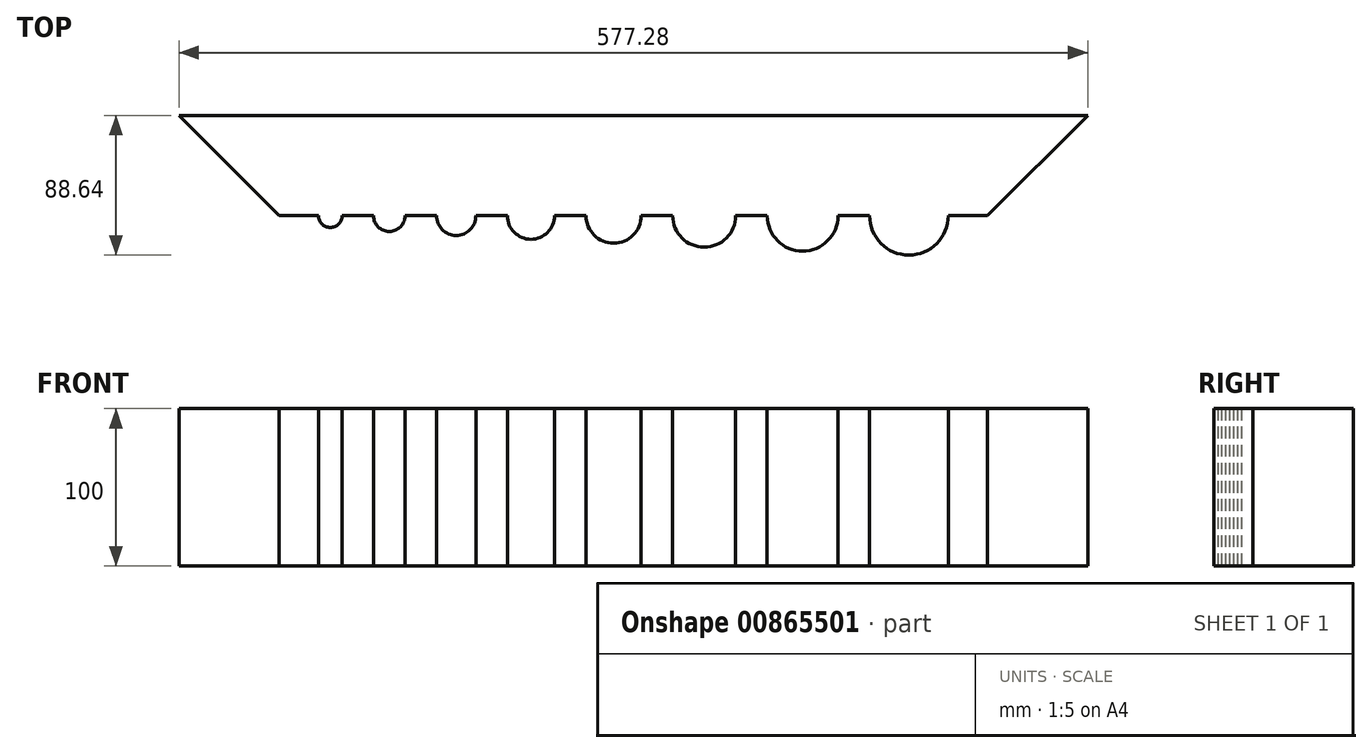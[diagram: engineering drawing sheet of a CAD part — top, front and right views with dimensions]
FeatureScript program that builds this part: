
annotation { "Feature Type Name" : "Feature", "Feature Type Description" : "" }
export const myFeature = defineFeature(function(context is Context, id is Id, definition is map)
    precondition{}
    {
        {
            var Q0;
            Q0=qCreatedBy(makeId("Top.planeOp"),FACE);
            var sketch = newSketch(context, id + "F0", { "sketchPlane" : qUnion([Q0])});
            skLineSegment(sketch, "E0.bottom", {"start": v(0, 0) * mm, "end": v(450, 0) * mm});
            skLineSegment(sketch, "E0.top", {"start": v(0, -450) * mm, "end": v(450, -450) * mm});
            skLineSegment(sketch, "E0.left", {"start": v(0, 0) * mm, "end": v(0, -450) * mm});
            skLineSegment(sketch, "E0.right", {"start": v(450, 0) * mm, "end": v(450, -450) * mm});
            skCircle(sketch, "E1", {"center": v(32.5, 0) * mm, "radius": 7.5 * mm});
            skCircle(sketch, "E2", {"center": v(70, 0) * mm, "radius": 10 * mm});
            skCircle(sketch, "E3", {"center": v(112.5, 0) * mm, "radius": 12.5 * mm});
            skCircle(sketch, "E4", {"center": v(212.5, 0) * mm, "radius": 17.5 * mm});
            skCircle(sketch, "E5", {"center": v(270, 0) * mm, "radius": 20 * mm});
            skPoint(sketch, "E6", {"position": v(0, -225) * mm});
            skCircle(sketch, "E7", {"center": v(160, 0) * mm, "radius": 15 * mm});
            skCircle(sketch, "E8", {"center": v(332.5, 0) * mm, "radius": 22.5 * mm});
            skCircle(sketch, "E9", {"center": v(400, 0) * mm, "radius": 25 * mm});
            skCircle(sketch, "E10", {"center": v(0, -50) * mm, "radius": 27.5 * mm});
            skCircle(sketch, "E11", {"center": v(0, -127.5) * mm, "radius": 30 * mm});
            skCircle(sketch, "E12", {"center": v(0, -210) * mm, "radius": 32.5 * mm});
            skCircle(sketch, "E13", {"center": v(0, -297.5) * mm, "radius": 35 * mm});
            skCircle(sketch, "E14", {"center": v(0, -390) * mm, "radius": 37.5 * mm});
            skCircle(sketch, "E15.cCircle", {"center": v(450, -45) * mm, "radius": 20 * mm, "construction": true});
            skLineSegment(sketch, "E15.0", {"start": v(450, -65) * mm, "end": v(432.68, -55) * mm});
            skLineSegment(sketch, "E15.1", {"start": v(432.68, -55) * mm, "end": v(432.68, -35) * mm});
            skLineSegment(sketch, "E15.2", {"start": v(432.68, -35) * mm, "end": v(450, -25) * mm});
            skLineSegment(sketch, "E15.3", {"start": v(450, -25) * mm, "end": v(467.32, -35) * mm});
            skLineSegment(sketch, "E15.4", {"start": v(467.32, -35) * mm, "end": v(467.32, -55) * mm});
            skLineSegment(sketch, "E15.5", {"start": v(467.32, -55) * mm, "end": v(450, -65) * mm});
            skCircle(sketch, "E16.cCircle", {"center": v(450, -120) * mm, "radius": 34.64 * mm, "construction": true});
            skLineSegment(sketch, "E16.0", {"start": v(420.17, -137.61) * mm, "end": v(419.83, -102.97) * mm});
            skLineSegment(sketch, "E16.1", {"start": v(419.83, -102.97) * mm, "end": v(449.66, -85.36) * mm});
            skLineSegment(sketch, "E16.2", {"start": v(449.66, -85.36) * mm, "end": v(479.83, -102.39) * mm});
            skLineSegment(sketch, "E16.3", {"start": v(479.83, -102.39) * mm, "end": v(480.17, -137.03) * mm});
            skLineSegment(sketch, "E16.4", {"start": v(480.17, -137.03) * mm, "end": v(450.34, -154.64) * mm});
            skLineSegment(sketch, "E16.5", {"start": v(450.34, -154.64) * mm, "end": v(420.17, -137.61) * mm});
            skCircle(sketch, "E17.cCircle", {"center": v(450, -225) * mm, "radius": 46.19 * mm, "construction": true});
            skLineSegment(sketch, "E17.0", {"start": v(410.35, -248.7) * mm, "end": v(409.66, -202.51) * mm});
            skLineSegment(sketch, "E17.1", {"start": v(409.66, -202.51) * mm, "end": v(449.3, -178.82) * mm});
            skLineSegment(sketch, "E17.2", {"start": v(449.3, -178.82) * mm, "end": v(489.65, -201.3) * mm});
            skLineSegment(sketch, "E17.3", {"start": v(489.65, -201.3) * mm, "end": v(490.34, -247.49) * mm});
            skLineSegment(sketch, "E17.4", {"start": v(490.34, -247.49) * mm, "end": v(450.7, -271.18) * mm});
            skLineSegment(sketch, "E17.5", {"start": v(450.7, -271.18) * mm, "end": v(410.35, -248.7) * mm});
            skCircle(sketch, "E18.cCircle", {"center": v(450, -360) * mm, "radius": 57.74 * mm, "construction": true});
            skLineSegment(sketch, "E18.0", {"start": v(400.24, -330.72) * mm, "end": v(450.48, -302.27) * mm});
            skLineSegment(sketch, "E18.1", {"start": v(450.48, -302.27) * mm, "end": v(500.24, -331.55) * mm});
            skLineSegment(sketch, "E18.2", {"start": v(500.24, -331.55) * mm, "end": v(499.76, -389.28) * mm});
            skLineSegment(sketch, "E18.3", {"start": v(499.76, -389.28) * mm, "end": v(449.52, -417.73) * mm});
            skLineSegment(sketch, "E18.4", {"start": v(449.52, -417.73) * mm, "end": v(399.76, -388.45) * mm});
            skLineSegment(sketch, "E18.5", {"start": v(399.76, -388.45) * mm, "end": v(400.24, -330.72) * mm});
            skLineSegment(sketch, "E19", {"start": v(420, -450) * mm, "end": v(412.5, -437) * mm});
            skLineSegment(sketch, "E20", {"start": v(412.5, -437) * mm, "end": v(405, -450) * mm});
            skLineSegment(sketch, "E21", {"start": v(420, -450) * mm, "end": v(405, -450) * mm});
            skLineSegment(sketch, "E22", {"start": v(375, -450) * mm, "end": v(362.5, -428.35) * mm});
            skLineSegment(sketch, "E23", {"start": v(362.5, -428.35) * mm, "end": v(350, -450) * mm});
            skLineSegment(sketch, "E24", {"start": v(350, -450) * mm, "end": v(375, -450) * mm});
            skLineSegment(sketch, "E25", {"start": v(320, -450) * mm, "end": v(305, -424.02) * mm});
            skLineSegment(sketch, "E26", {"start": v(305, -424.02) * mm, "end": v(290, -450) * mm});
            skLineSegment(sketch, "E27", {"start": v(290, -450) * mm, "end": v(320, -450) * mm});
            skLineSegment(sketch, "E28", {"start": v(260, -450) * mm, "end": v(220, -450) * mm});
            skLineSegment(sketch, "E29", {"start": v(220, -450) * mm, "end": v(240, -415.36) * mm});
            skLineSegment(sketch, "E30", {"start": v(240, -415.36) * mm, "end": v(260, -450) * mm});
            skLineSegment(sketch, "E31", {"start": v(190, -450) * mm, "end": v(140, -450) * mm});
            skLineSegment(sketch, "E32", {"start": v(140, -450) * mm, "end": v(165, -406.7) * mm});
            skLineSegment(sketch, "E33", {"start": v(165, -406.7) * mm, "end": v(190, -450) * mm});
            skLineSegment(sketch, "E34", {"start": v(110, -450) * mm, "end": v(50, -450) * mm});
            skLineSegment(sketch, "E35", {"start": v(50, -450) * mm, "end": v(80, -398.04) * mm});
            skLineSegment(sketch, "E36", {"start": v(80, -398.04) * mm, "end": v(110, -450) * mm});
            skCircle(sketch, "E37", {"center": v(366.86, -63.19) * mm, "radius": 8.5 * mm});
            skCircle(sketch, "E38", {"center": v(306.86, -63.19) * mm, "radius": 11.5 * mm});
            skCircle(sketch, "E39", {"center": v(237.86, -63.19) * mm, "radius": 17.5 * mm});
            skCircle(sketch, "E40", {"center": v(172.86, -63.19) * mm, "radius": 22.5 * mm});
            skCircle(sketch, "E41", {"center": v(90.36, -63.19) * mm, "radius": 30 * mm});
            skPoint(sketch, "E42.cornerSnap0", {"position": v(400, -359.59) * mm});
            skEllipse(sketch, "E43", {"center": v(355, -158.3) * mm, "majorRadius": 69.57 * mm, "minorRadius": 24.91 * mm, "majorAxis": v(0, -1)});
            skEllipse(sketch, "E44", {"center": v(255, -158.3) * mm, "majorRadius": 57.98 * mm, "minorRadius": 25.3 * mm, "majorAxis": v(0, -1)});
            skEllipse(sketch, "E45", {"center": v(160, -158.3) * mm, "majorRadius": 47.06 * mm, "minorRadius": 19.98 * mm, "majorAxis": v(0, -1)});
            skEllipse(sketch, "E46", {"center": v(75, -158.3) * mm, "majorRadius": 42.97 * mm, "minorRadius": 16.37 * mm, "majorAxis": v(0, -1)});
            skLineSegment(sketch, "E47.bottom", {"start": v(132.9, -316.06) * mm, "end": v(52.9, -316.06) * mm});
            skLineSegment(sketch, "E47.top", {"start": v(132.9, -236.06) * mm, "end": v(52.9, -236.06) * mm});
            skLineSegment(sketch, "E47.left", {"start": v(132.9, -316.06) * mm, "end": v(132.9, -236.06) * mm});
            skLineSegment(sketch, "E47.right", {"start": v(52.9, -316.06) * mm, "end": v(52.9, -236.06) * mm});
            skPoint(sketch, "E47.middle", {"position": v(92.9, -276.06) * mm});
            skLineSegment(sketch, "E48.bottom", {"start": v(232.94, -306.06) * mm, "end": v(172.94, -306.06) * mm});
            skLineSegment(sketch, "E48.top", {"start": v(232.94, -246.06) * mm, "end": v(172.94, -246.06) * mm});
            skLineSegment(sketch, "E48.left", {"start": v(232.94, -306.06) * mm, "end": v(232.94, -246.06) * mm});
            skLineSegment(sketch, "E48.right", {"start": v(172.94, -306.06) * mm, "end": v(172.94, -246.06) * mm});
            skPoint(sketch, "E48.middle", {"position": v(202.94, -276.06) * mm});
            skLineSegment(sketch, "E49.bottom", {"start": v(312.28, -296.06) * mm, "end": v(272.28, -296.06) * mm});
            skLineSegment(sketch, "E49.top", {"start": v(312.28, -256.06) * mm, "end": v(272.28, -256.06) * mm});
            skLineSegment(sketch, "E49.left", {"start": v(312.28, -296.06) * mm, "end": v(312.28, -256.06) * mm});
            skLineSegment(sketch, "E49.right", {"start": v(272.28, -296.06) * mm, "end": v(272.28, -256.06) * mm});
            skPoint(sketch, "E49.middle", {"position": v(292.28, -276.06) * mm});
            skLineSegment(sketch, "E50.bottom", {"start": v(372.3, -286.06) * mm, "end": v(352.3, -286.06) * mm});
            skLineSegment(sketch, "E50.top", {"start": v(372.3, -266.06) * mm, "end": v(352.3, -266.06) * mm});
            skLineSegment(sketch, "E50.left", {"start": v(372.3, -286.06) * mm, "end": v(372.3, -266.06) * mm});
            skLineSegment(sketch, "E50.right", {"start": v(352.3, -286.06) * mm, "end": v(352.3, -266.06) * mm});
            skPoint(sketch, "E50.middle", {"position": v(362.3, -276.06) * mm});
            skLineSegment(sketch, "E51.bottom", {"start": v(80, -382.47) * mm, "end": v(60, -382.47) * mm});
            skLineSegment(sketch, "E51.top", {"start": v(80, -372.47) * mm, "end": v(60, -372.47) * mm});
            skLineSegment(sketch, "E51.left", {"start": v(80, -382.47) * mm, "end": v(80, -372.47) * mm});
            skLineSegment(sketch, "E51.right", {"start": v(60, -382.47) * mm, "end": v(60, -372.47) * mm});
            skPoint(sketch, "E51.middle", {"position": v(70, -377.47) * mm});
            skLineSegment(sketch, "E52.bottom", {"start": v(110, -387.47) * mm, "end": v(150, -387.47) * mm});
            skLineSegment(sketch, "E52.top", {"start": v(110, -367.47) * mm, "end": v(150, -367.47) * mm});
            skLineSegment(sketch, "E52.left", {"start": v(110, -387.47) * mm, "end": v(110, -367.47) * mm});
            skLineSegment(sketch, "E52.right", {"start": v(150, -387.47) * mm, "end": v(150, -367.47) * mm});
            skPoint(sketch, "E52.middle", {"position": v(130, -377.47) * mm});
            skLineSegment(sketch, "E53.bottom", {"start": v(190, -392.47) * mm, "end": v(250, -392.47) * mm});
            skLineSegment(sketch, "E53.top", {"start": v(190, -362.47) * mm, "end": v(250, -362.47) * mm});
            skLineSegment(sketch, "E53.left", {"start": v(190, -392.47) * mm, "end": v(190, -362.47) * mm});
            skLineSegment(sketch, "E53.right", {"start": v(250, -392.47) * mm, "end": v(250, -362.47) * mm});
            skPoint(sketch, "E53.middle", {"position": v(220, -377.47) * mm});
            skLineSegment(sketch, "E54.bottom", {"start": v(375, -397.47) * mm, "end": v(295, -397.47) * mm});
            skLineSegment(sketch, "E54.top", {"start": v(375, -357.47) * mm, "end": v(295, -357.47) * mm});
            skLineSegment(sketch, "E54.left", {"start": v(375, -397.47) * mm, "end": v(375, -357.47) * mm});
            skLineSegment(sketch, "E54.right", {"start": v(295, -397.47) * mm, "end": v(295, -357.47) * mm});
            skPoint(sketch, "E54.middle", {"position": v(335, -377.47) * mm});
            skLineSegment(sketch, "E55", {"start": v(0, 0) * mm, "end": v(-63.64, 63.64) * mm});
            skLineSegment(sketch, "E56", {"start": v(-63.64, 63.64) * mm, "end": v(513.64, 63.64) * mm});
            skLineSegment(sketch, "E57", {"start": v(513.64, 63.64) * mm, "end": v(450, 0) * mm});
            skLineSegment(sketch, "E58", {"start": v(513.64, 63.64) * mm, "end": v(513.64, -513.64) * mm});
            skLineSegment(sketch, "E59", {"start": v(513.64, -513.64) * mm, "end": v(450, -450) * mm});
            skLineSegment(sketch, "E60", {"start": v(-63.64, 63.64) * mm, "end": v(-63.64, -513.64) * mm});
            skLineSegment(sketch, "E61", {"start": v(-63.64, -513.64) * mm, "end": v(0, -450) * mm});
            skLineSegment(sketch, "E62", {"start": v(-63.64, -513.64) * mm, "end": v(513.64, -513.64) * mm});
            skSolve(sketch);
        }
        {
            var Q0;
            {var subQ20=sQuery(id+"F0.wireOp",EDGE,"E55");Q0=makeQuery(id+"F0.imprint","IMPRINT",FACE,{"disambiguationData":[TD([[makeQuery(id+"F0.imprint","IMPRINT",EDGE,{"derivedFrom":subQ20}),-1.0]])]});}
            var Q1;
            {var subQ0=sQuery(id+"F0.wireOp",EDGE,"E1");var subQ1=sQuery(id+"F0.wireOp",EDGE,"E0.bottom");var subQ2=makeQuery(id+"F0.imprint","INTERSECT",VERTEX,{"disambiguationData":[OD(0.0)],"derivedFrom":[subQ1,subQ0]});Q1=makeQuery(id+"F0.imprint","IMPRINT",FACE,{"disambiguationData":[TD([[makeQuery(id+"F0.imprint","IMPRINT",EDGE,{"disambiguationData":[TD([[subQ2,-1.0]])],"derivedFrom":subQ1}),1.0]])]});}
            var Q2;
            {var subQ0=sQuery(id+"F0.wireOp",EDGE,"E1");var subQ1=sQuery(id+"F0.wireOp",EDGE,"E0.bottom");var subQ2=makeQuery(id+"F0.imprint","INTERSECT",VERTEX,{"disambiguationData":[OD(0.0)],"derivedFrom":[subQ1,subQ0]});Q2=makeQuery(id+"F0.imprint","IMPRINT",FACE,{"disambiguationData":[TD([[makeQuery(id+"F0.imprint","IMPRINT",EDGE,{"disambiguationData":[TD([[subQ2,-1.0]])],"derivedFrom":subQ1}),-1.0]])]});}
            var Q3;
            {var subQ0=sQuery(id+"F0.wireOp",EDGE,"E2");var subQ1=sQuery(id+"F0.wireOp",EDGE,"E0.bottom");var subQ2=makeQuery(id+"F0.imprint","INTERSECT",VERTEX,{"disambiguationData":[OD(0.0)],"derivedFrom":[subQ1,subQ0]});Q3=makeQuery(id+"F0.imprint","IMPRINT",FACE,{"disambiguationData":[TD([[makeQuery(id+"F0.imprint","IMPRINT",EDGE,{"disambiguationData":[TD([[subQ2,-1.0]])],"derivedFrom":subQ1}),1.0]])]});}
            var Q4;
            {var subQ0=sQuery(id+"F0.wireOp",EDGE,"E2");var subQ1=sQuery(id+"F0.wireOp",EDGE,"E0.bottom");var subQ2=makeQuery(id+"F0.imprint","INTERSECT",VERTEX,{"disambiguationData":[OD(0.0)],"derivedFrom":[subQ1,subQ0]});Q4=makeQuery(id+"F0.imprint","IMPRINT",FACE,{"disambiguationData":[TD([[makeQuery(id+"F0.imprint","IMPRINT",EDGE,{"disambiguationData":[TD([[subQ2,-1.0]])],"derivedFrom":subQ1}),-1.0]])]});}
            var Q5;
            {var subQ0=sQuery(id+"F0.wireOp",EDGE,"E3");var subQ1=sQuery(id+"F0.wireOp",EDGE,"E0.bottom");var subQ2=makeQuery(id+"F0.imprint","INTERSECT",VERTEX,{"disambiguationData":[OD(0.0)],"derivedFrom":[subQ1,subQ0]});Q5=makeQuery(id+"F0.imprint","IMPRINT",FACE,{"disambiguationData":[TD([[makeQuery(id+"F0.imprint","IMPRINT",EDGE,{"disambiguationData":[TD([[subQ2,-1.0]])],"derivedFrom":subQ1}),-1.0]])]});}
            var Q6;
            {var subQ0=sQuery(id+"F0.wireOp",EDGE,"E3");var subQ1=sQuery(id+"F0.wireOp",EDGE,"E0.bottom");var subQ2=makeQuery(id+"F0.imprint","INTERSECT",VERTEX,{"disambiguationData":[OD(0.0)],"derivedFrom":[subQ1,subQ0]});Q6=makeQuery(id+"F0.imprint","IMPRINT",FACE,{"disambiguationData":[TD([[makeQuery(id+"F0.imprint","IMPRINT",EDGE,{"disambiguationData":[TD([[subQ2,-1.0]])],"derivedFrom":subQ1}),1.0]])]});}
            var Q7;
            {var subQ0=sQuery(id+"F0.wireOp",EDGE,"E7");var subQ1=sQuery(id+"F0.wireOp",EDGE,"E0.bottom");var subQ2=makeQuery(id+"F0.imprint","INTERSECT",VERTEX,{"disambiguationData":[OD(0.0)],"derivedFrom":[subQ1,subQ0]});Q7=makeQuery(id+"F0.imprint","IMPRINT",FACE,{"disambiguationData":[TD([[makeQuery(id+"F0.imprint","IMPRINT",EDGE,{"disambiguationData":[TD([[subQ2,-1.0]])],"derivedFrom":subQ1}),-1.0]])]});}
            var Q8;
            {var subQ0=sQuery(id+"F0.wireOp",EDGE,"E7");var subQ1=sQuery(id+"F0.wireOp",EDGE,"E0.bottom");var subQ2=makeQuery(id+"F0.imprint","INTERSECT",VERTEX,{"disambiguationData":[OD(0.0)],"derivedFrom":[subQ1,subQ0]});Q8=makeQuery(id+"F0.imprint","IMPRINT",FACE,{"disambiguationData":[TD([[makeQuery(id+"F0.imprint","IMPRINT",EDGE,{"disambiguationData":[TD([[subQ2,-1.0]])],"derivedFrom":subQ1}),1.0]])]});}
            var Q9;
            {var subQ0=sQuery(id+"F0.wireOp",EDGE,"E4");var subQ1=sQuery(id+"F0.wireOp",EDGE,"E0.bottom");var subQ2=makeQuery(id+"F0.imprint","INTERSECT",VERTEX,{"disambiguationData":[OD(0.0)],"derivedFrom":[subQ1,subQ0]});Q9=makeQuery(id+"F0.imprint","IMPRINT",FACE,{"disambiguationData":[TD([[makeQuery(id+"F0.imprint","IMPRINT",EDGE,{"disambiguationData":[TD([[subQ2,-1.0]])],"derivedFrom":subQ1}),-1.0]])]});}
            var Q10;
            {var subQ0=sQuery(id+"F0.wireOp",EDGE,"E4");var subQ1=sQuery(id+"F0.wireOp",EDGE,"E0.bottom");var subQ2=makeQuery(id+"F0.imprint","INTERSECT",VERTEX,{"disambiguationData":[OD(0.0)],"derivedFrom":[subQ1,subQ0]});Q10=makeQuery(id+"F0.imprint","IMPRINT",FACE,{"disambiguationData":[TD([[makeQuery(id+"F0.imprint","IMPRINT",EDGE,{"disambiguationData":[TD([[subQ2,-1.0]])],"derivedFrom":subQ1}),1.0]])]});}
            var Q11;
            {var subQ0=sQuery(id+"F0.wireOp",EDGE,"E5");var subQ1=sQuery(id+"F0.wireOp",EDGE,"E0.bottom");var subQ2=makeQuery(id+"F0.imprint","INTERSECT",VERTEX,{"disambiguationData":[OD(0.0)],"derivedFrom":[subQ1,subQ0]});Q11=makeQuery(id+"F0.imprint","IMPRINT",FACE,{"disambiguationData":[TD([[makeQuery(id+"F0.imprint","IMPRINT",EDGE,{"disambiguationData":[TD([[subQ2,-1.0]])],"derivedFrom":subQ1}),-1.0]])]});}
            var Q12;
            {var subQ0=sQuery(id+"F0.wireOp",EDGE,"E5");var subQ1=sQuery(id+"F0.wireOp",EDGE,"E0.bottom");var subQ2=makeQuery(id+"F0.imprint","INTERSECT",VERTEX,{"disambiguationData":[OD(0.0)],"derivedFrom":[subQ1,subQ0]});Q12=makeQuery(id+"F0.imprint","IMPRINT",FACE,{"disambiguationData":[TD([[makeQuery(id+"F0.imprint","IMPRINT",EDGE,{"disambiguationData":[TD([[subQ2,-1.0]])],"derivedFrom":subQ1}),1.0]])]});}
            var Q13;
            {var subQ0=sQuery(id+"F0.wireOp",EDGE,"E8");var subQ1=sQuery(id+"F0.wireOp",EDGE,"E0.bottom");var subQ2=makeQuery(id+"F0.imprint","INTERSECT",VERTEX,{"disambiguationData":[OD(0.0)],"derivedFrom":[subQ1,subQ0]});Q13=makeQuery(id+"F0.imprint","IMPRINT",FACE,{"disambiguationData":[TD([[makeQuery(id+"F0.imprint","IMPRINT",EDGE,{"disambiguationData":[TD([[subQ2,-1.0]])],"derivedFrom":subQ1}),-1.0]])]});}
            var Q14;
            {var subQ0=sQuery(id+"F0.wireOp",EDGE,"E8");var subQ1=sQuery(id+"F0.wireOp",EDGE,"E0.bottom");var subQ2=makeQuery(id+"F0.imprint","INTERSECT",VERTEX,{"disambiguationData":[OD(0.0)],"derivedFrom":[subQ1,subQ0]});Q14=makeQuery(id+"F0.imprint","IMPRINT",FACE,{"disambiguationData":[TD([[makeQuery(id+"F0.imprint","IMPRINT",EDGE,{"disambiguationData":[TD([[subQ2,-1.0]])],"derivedFrom":subQ1}),1.0]])]});}
            var Q15;
            {var subQ0=sQuery(id+"F0.wireOp",EDGE,"E9");var subQ1=sQuery(id+"F0.wireOp",EDGE,"E0.bottom");var subQ2=makeQuery(id+"F0.imprint","INTERSECT",VERTEX,{"disambiguationData":[OD(0.0)],"derivedFrom":[subQ1,subQ0]});Q15=makeQuery(id+"F0.imprint","IMPRINT",FACE,{"disambiguationData":[TD([[makeQuery(id+"F0.imprint","IMPRINT",EDGE,{"disambiguationData":[TD([[subQ2,-1.0]])],"derivedFrom":subQ1}),-1.0]])]});}
            var Q16;
            {var subQ0=sQuery(id+"F0.wireOp",EDGE,"E9");var subQ1=sQuery(id+"F0.wireOp",EDGE,"E0.bottom");var subQ2=makeQuery(id+"F0.imprint","INTERSECT",VERTEX,{"disambiguationData":[OD(0.0)],"derivedFrom":[subQ1,subQ0]});Q16=makeQuery(id+"F0.imprint","IMPRINT",FACE,{"disambiguationData":[TD([[makeQuery(id+"F0.imprint","IMPRINT",EDGE,{"disambiguationData":[TD([[subQ2,-1.0]])],"derivedFrom":subQ1}),1.0]])]});}
            extrude(context, id + "F1", {"entities" : qUnion([Q0, Q1, Q2, Q3, Q4, Q5, Q6, Q7, Q8, Q9, Q10, Q11, Q12, Q13, Q14, Q15, Q16]), "depth" : 100 * mm, "offsetDistance" : 25 * mm});
        }
    });
